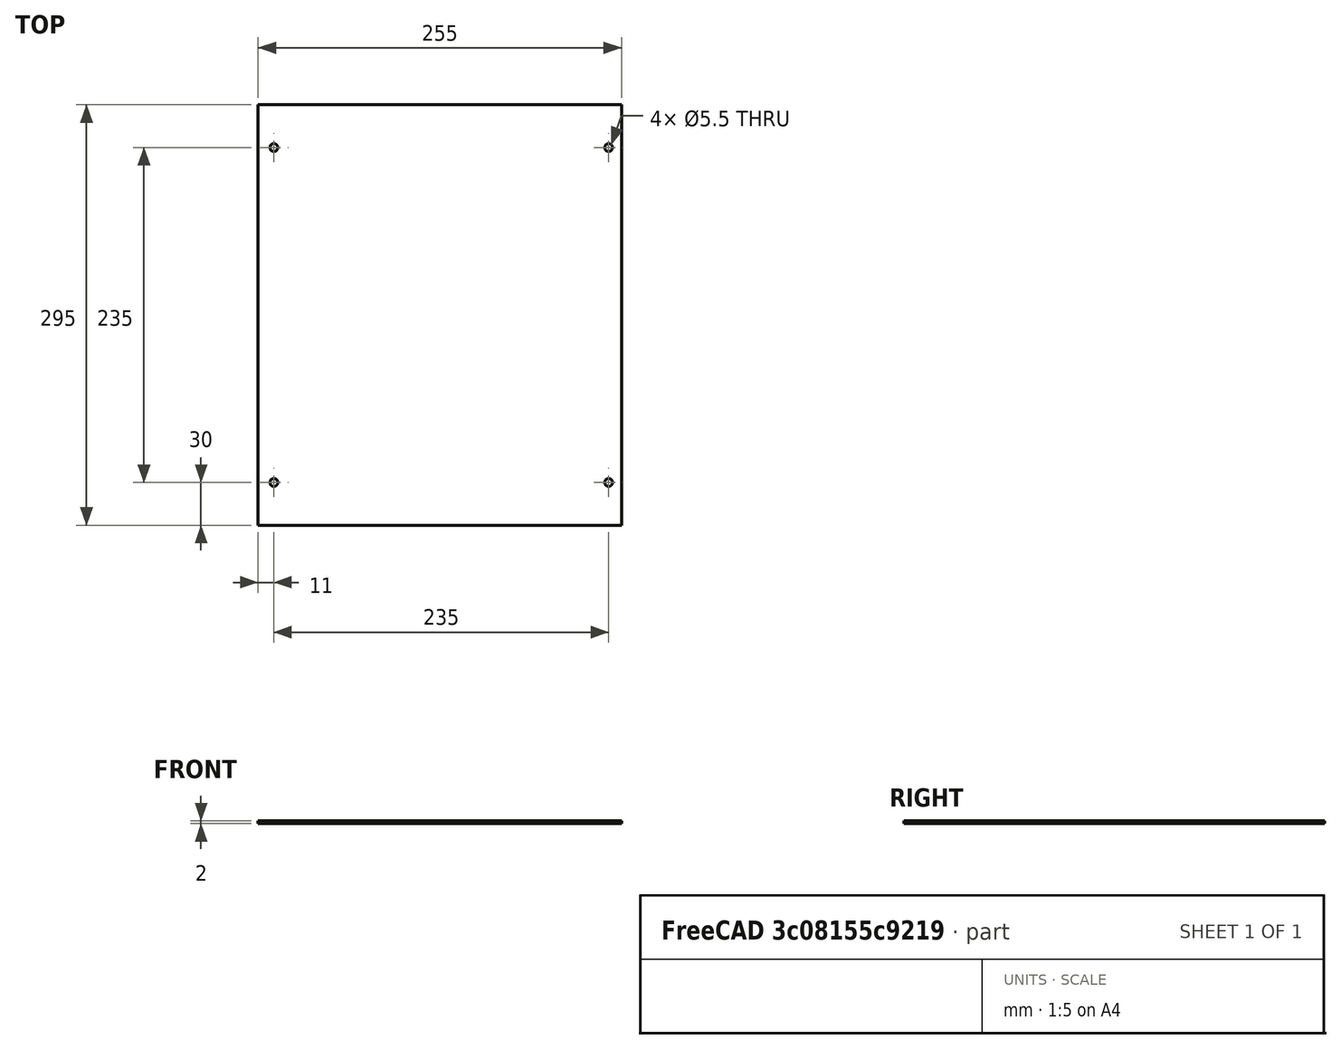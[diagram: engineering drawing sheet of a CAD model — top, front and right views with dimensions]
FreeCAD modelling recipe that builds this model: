
FCSTD DOCUMENT  (FreeCAD 0.15R4671 (Git))
Label: bottom
License: All rights reserved
LicenseURL: http://en.wikipedia.org/wiki/All_rights_reserved
objects: Drawing::FeatureViewPython×5, Part::Cylinder×4, Part::Cut×4, Part::Box×1, Drawing::FeatureViewPart×1, Drawing::FeaturePage×1
note: 9 computed .brp shape members not serialized (recipe doc carries the construction recipe); baked Part::Feature solids carry a one-line shape summary decoded from their .brp

FEATURE [Part::Box] Box  label="Cube"
  Height = 2
  Length = 255
  Placement = pos=(-1,0,1.5332e-08) rot=(0,0,1;0rad)
  Width = 295
FEATURE [Part::Cylinder] Cylinder
  Angle = 360
  Height = 10
  Placement = pos=(10,30,-5) rot=(0,0,1;0rad)
  Radius = 2.75
FEATURE [Part::Cylinder] Cylinder001
  Angle = 360
  Height = 10
  Placement = pos=(10,265,-5) rot=(0,0,1;0rad)
  Radius = 2.75
FEATURE [Part::Cylinder] Cylinder002
  Angle = 360
  Height = 10
  Placement = pos=(245,30,-5) rot=(0,0,1;0rad)
  Radius = 2.75
FEATURE [Part::Cylinder] Cylinder003
  Angle = 360
  Height = 10
  Placement = pos=(245,265,-5) rot=(0,0,1;0rad)
  Radius = 2.75
FEATURE [Part::Cut] Cut
  Base = -> Box
  Tool = -> Cylinder
FEATURE [Part::Cut] Cut001
  Base = -> Cut
  Tool = -> Cylinder001
FEATURE [Part::Cut] Cut002
  Base = -> Cut001
  Tool = -> Cylinder002
FEATURE [Part::Cut] Cut003  label="bottom"
  Base = -> Cut002
  Tool = -> Cylinder003
FEATURE [Drawing::FeatureViewPart] Ortho  label="Ortho_0_0"
  Direction = (0,0,1)
  HiddenWidth = 0.15
  LineWidth = 0.35
  Rotation = 0
  Scale = 0.5
  ShowHiddenLines = false
  ShowSmoothLines = false
  Source = -> Cut003
  Tolerance = 0.05
  ViewResult = <g id="Ortho_0_0"\n   transform="rotate(0,46.75,192.25) translate(46.75,192.25) scale(0.5,0.5)"\n  >\n<g   stroke="rgb(0, 0, 0)"\n   stroke-width="0.7"\n   stroke-linecap="butt"\n   stroke-linejoin="miter"\n   fill="none"\n   transform="scale(1,-1)"\n  >\n<path id= "1" d=" M -1 0 L -1 295 " />\n<path id= "2" d=" M -1 0 L 254 0 " />\n<path id= "3" d=" M -1 295 L 254 295 " />\n<path id= "4" d=" M 254 0 L 254 295 " />\n<circle cx ="245" cy ="265" r ="2.75" /><circle cx ="10" cy ="265" r ="2.75" /><circle cx ="245" cy ="30" r ="2.75" /><circle cx ="10" cy ="30" r ="2.75" /></g>\n</g>
  Visible = true
  X = 46.75
  Y = 192.25
FEATURE [Drawing::FeatureViewPython] dim001  # drawing view (typed FeaturePython)
  Rotation = 0
  ViewResult = <g> \n  <line x1="44.250000" y1="192.250000" x2="32.753277" y2="192.250000" style="stroke:rgb(0,0,255);stroke-width:0.50" />\n<line x1="44.250000" y1="44.750000" x2="32.753277" y2="44.750000" style="stroke:rgb(0,0,255);stroke-width:0.50" />\n<line x1="33.753277" y1="192.250000" x2="33.753277" y2="44.750000" style="stroke:rgb(0,0,255);stroke-width:0.50" /> \n  <polygon points="33.753277,44.750000 32.753277,47.750000 33.753277,48.750000 34.753277,47.750000" style="fill:rgb(0,0,255);stroke:rgb(0,0,255);stroke-width:0" /><polygon points="33.753277,192.250000 34.753277,189.250000 33.753277,188.250000 32.753277,189.250000" style="fill:rgb(0,0,255);stroke:rgb(0,0,255);stroke-width:0" /> \n  <text x="31.753277" y="118.500000" font-family="inherit" font-size="3.6" fill="rgb(0,0,255)" text-anchor="middle" transform="rotate(-90.000000 31.753277,118.500000)" >295</text> </g>
  Visible = true
  X = 0
  Y = 0
  arrowL1 = 3
  arrowL2 = 1
  arrowW = 2
  arrow_scheme = 0
  autoPlaceOffset = 2
  autoPlaceText = true
  click1_x = 33.7533
  click1_y = 114.839
  click2_x = 33.7533
  click2_y = 114.839
  comma_decimal_place = false
  dimension_line_overshoot = 1
  gap_datum_points = 2
  halfDimension_linear = false
  lineColor = rgb(0,0,255)
  strokeWidth = 0.5
  textFormat_linear = 295
  textRenderer_color = rgb(0,0,255)
  textRenderer_family = inherit
  textRenderer_size = 3.6
  unit_custom_scale = 1.2
  unit_scheme = 4
FEATURE [Drawing::FeatureViewPython] dim002  # drawing view (typed FeaturePython)
  Rotation = 0
  ViewResult = <g> \n  <line x1="46.250000" y1="42.750000" x2="46.250000" y2="30.425465" style="stroke:rgb(0,0,255);stroke-width:0.50" />\n<line x1="173.750000" y1="42.750000" x2="173.750000" y2="30.425465" style="stroke:rgb(0,0,255);stroke-width:0.50" />\n<line x1="46.250000" y1="31.425465" x2="173.750000" y2="31.425465" style="stroke:rgb(0,0,255);stroke-width:0.50" /> \n  <polygon points="173.750000,31.425465 170.750000,30.425465 169.750000,31.425465 170.750000,32.425465" style="fill:rgb(0,0,255);stroke:rgb(0,0,255);stroke-width:0" /><polygon points="46.250000,31.425465 49.250000,32.425465 50.250000,31.425465 49.250000,30.425465" style="fill:rgb(0,0,255);stroke:rgb(0,0,255);stroke-width:0" /> \n  <text x="110.000000" y="29.425465" font-family="inherit" font-size="3.6" fill="rgb(0,0,255)" text-anchor="middle" transform="rotate(0.000000 110.000000,29.425465)" >255</text> </g>
  Visible = true
  X = 0
  Y = 0
  arrowL1 = 3
  arrowL2 = 1
  arrowW = 2
  arrow_scheme = 0
  autoPlaceOffset = 2
  autoPlaceText = true
  click1_x = 100.484
  click1_y = 31.4255
  click2_x = 100.484
  click2_y = 31.4255
  comma_decimal_place = false
  dimension_line_overshoot = 1
  gap_datum_points = 2
  halfDimension_linear = false
  lineColor = rgb(0,0,255)
  strokeWidth = 0.5
  textFormat_linear = 255
  textRenderer_color = rgb(0,0,255)
  textRenderer_family = inherit
  textRenderer_size = 3.6
  unit_custom_scale = 1.2
  unit_scheme = 4
FEATURE [Drawing::FeatureViewPython] dia001  # drawing view (typed FeaturePython)
  Rotation = 0
  ViewResult = <g>  <circle cx ="169.250000" cy ="59.750000" r="0.250000" stroke="none" fill="rgb(0,0,255)" /> \n<line x1="188.940757" y1="59.747180" x2="167.875000" y2="59.750197" style="stroke:rgb(0,0,255);stroke-width:0.50" />\n<polygon points="170.625000,59.749803 173.625143,60.749373 174.625000,59.749230 173.624857,58.749373" style="fill:rgb(0,0,255);stroke:rgb(0,0,255);stroke-width:0" />\n<polygon points="167.875000,59.750197 164.874857,58.750627 163.875000,59.750770 164.875143,60.750627" style="fill:rgb(0,0,255);stroke:rgb(0,0,255);stroke-width:0" />\n<line x1="188.940757" y1="59.747180" x2="186.224976" y2="59.747180" style="stroke:rgb(0,0,255);stroke-width:0.50" />\n<text x="187.582867" y="57.747180" font-family="inherit" font-size="3.6" fill="rgb(0,0,255)" text-anchor="middle" transform="rotate(0.000000 187.582867,57.747180)" >Ø5.5</text> </g>
  Visible = true
  X = 0
  Y = 0
  arrowL1 = 3
  arrowL2 = 1
  arrowW = 2
  arrow_scheme = 0
  autoPlaceOffset = 2
  autoPlaceText = true
  centerPointDia = 0.5
  click1_x = 188.941
  click1_y = 59.7472
  click2_x = 186.225
  click2_y = 61.2991
  click3_x = 186.225
  click3_y = 61.2991
  comma_decimal_place = false
  lineColor = rgb(0,0,255)
  strokeWidth = 0.5
  textFormat_circular = Ø5.5
  textRenderer_color = rgb(0,0,255)
  textRenderer_family = inherit
  textRenderer_size = 3.6
  unit_custom_scale = 1.2
  unit_scheme = 4
FEATURE [Drawing::FeatureViewPython] dimStack001  # drawing view (typed FeaturePython)
  Rotation = 0
  ViewResult = <g> <line x1="172.625001" y1="177.250000" x2="181.862466" y2="177.250000" style="stroke:rgb(0,0,255);stroke-width:0.50" />\n<line x1="175.750001" y1="192.250000" x2="181.862466" y2="192.250000" style="stroke:rgb(0,0,255);stroke-width:0.50" />\n<line x1="180.862466" y1="177.250000" x2="180.862466" y2="192.250000" style="stroke:rgb(0,0,255);stroke-width:0.50" />\n<polygon points="180.862466,177.250000 179.862466,180.250000 180.862466,181.250000 181.862466,180.250000" style="fill:rgb(0,0,255);stroke:rgb(0,0,255);stroke-width:0" />\n<polygon points="180.862466,192.250000 181.862466,189.250000 180.862466,188.250000 179.862466,189.250000" style="fill:rgb(0,0,255);stroke:rgb(0,0,255);stroke-width:0" />\n<text x="178.862466" y="184.750000" font-family="inherit" font-size="3.6" fill="rgb(0,0,255)" text-anchor="middle" transform="rotate(-90.000000 178.862466,184.750000)" >30</text> </g> 
  Visible = true
  X = 0
  Y = 0
  arrowL1 = 3
  arrowL2 = 1
  arrowW = 2
  arrow_scheme = 0
  autoPlaceOffset = 2
  click1_x = 180.862
  click1_y = 186.449
  comma_decimal_place = false
  dimension_line_overshoot = 1
  gap_datum_points = 2
  lineColor = rgb(0,0,255)
  stack_offset = 7
  stack_offset0 = 0
  strokeWidth = 0.5
  textFormat_linear = 30
  textRenderer_color = rgb(0,0,255)
  textRenderer_family = inherit
  textRenderer_size = 3.6
  unit_custom_scale = 1.2
  unit_scheme = 4
FEATURE [Drawing::FeatureViewPython] dimStack002  # drawing view (typed FeaturePython)
  Rotation = 0
  ViewResult = <g> <line x1="169.250000" y1="180.625001" x2="169.250000" y2="204.340345" style="stroke:rgb(0,0,255);stroke-width:0.50" />\n<line x1="173.750000" y1="194.250001" x2="173.750000" y2="204.340345" style="stroke:rgb(0,0,255);stroke-width:0.50" />\n<line x1="169.250000" y1="203.340345" x2="173.750000" y2="203.340345" style="stroke:rgb(0,0,255);stroke-width:0.50" />\n<polygon points="169.250000,203.340345 166.250000,202.340345 165.250000,203.340345 166.250000,204.340345" style="fill:rgb(0,0,255);stroke:rgb(0,0,255);stroke-width:0" />\n<polygon points="173.750000,203.340345 176.750000,204.340345 177.750000,203.340345 176.750000,202.340345" style="fill:rgb(0,0,255);stroke:rgb(0,0,255);stroke-width:0" />\n<text x="171.500000" y="201.340345" font-family="inherit" font-size="3.6" fill="rgb(0,0,255)" text-anchor="middle" transform="rotate(0.000000 171.500000,201.340345)" >10</text> </g> 
  Visible = true
  X = 0
  Y = 0
  arrowL1 = 3
  arrowL2 = 1
  arrowW = 2
  arrow_scheme = 0
  autoPlaceOffset = 2
  click1_x = 173.846
  click1_y = 203.34
  comma_decimal_place = false
  dimension_line_overshoot = 1
  gap_datum_points = 2
  lineColor = rgb(0,0,255)
  stack_offset = 7
  stack_offset0 = 0
  strokeWidth = 0.5
  textFormat_linear = 10
  textRenderer_color = rgb(0,0,255)
  textRenderer_family = inherit
  textRenderer_size = 3.6
  unit_custom_scale = 1.2
  unit_scheme = 4
FEATURE [Drawing::FeaturePage] Page
  EditableTexts = Fichou Dimitri | OCLab bottom | Aluminium - 2 mm thick | Professur für Lebensmittelwissenschaften | Prof. Dr. Gertrud Morlock | A4 | X / Y | SCALE | PART NUMBER | DRAWING NUMBER | YYYY-MM-DD | A
  Group = -> [Ortho,dim001,dim002,dia001,dimStack001,dimStack002]
  Template = <path>
note: 1 file-system path scrubbed to <path> (originals preserved in the JSON sidecar)
